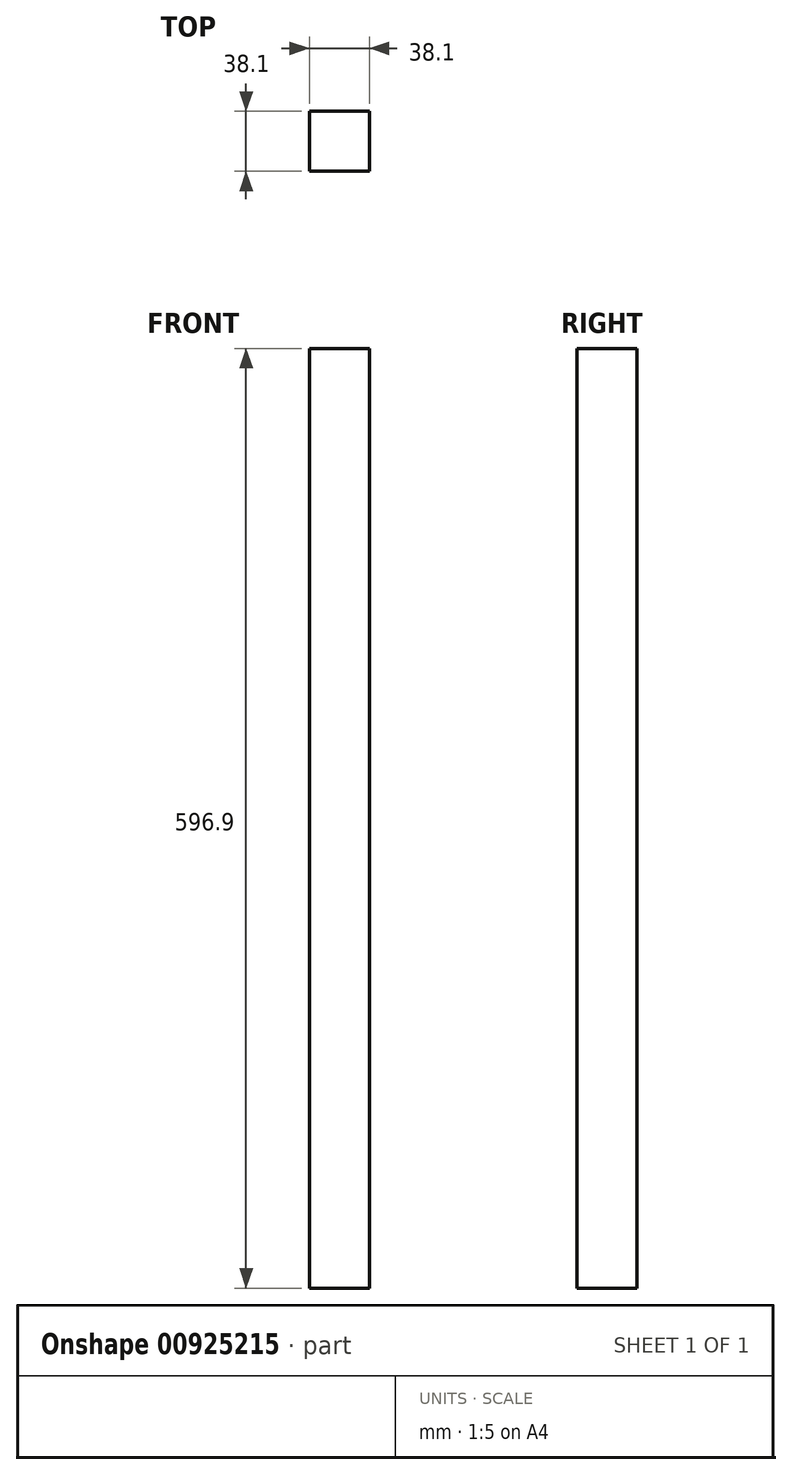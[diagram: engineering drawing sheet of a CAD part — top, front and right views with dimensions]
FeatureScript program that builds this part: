
annotation { "Feature Type Name" : "Feature", "Feature Type Description" : "" }
export const myFeature = defineFeature(function(context is Context, id is Id, definition is map)
    precondition{}
    {
        {
            var Q0;
            Q0=qCreatedBy(makeId("Top.planeOp"),FACE);
            var sketch = newSketch(context, id + "F0", { "sketchPlane" : qUnion([Q0])});
            skLineSegment(sketch, "E0.bottom", {"start": v(19.05, -19.05) * mm, "end": v(-19.05, -19.05) * mm});
            skLineSegment(sketch, "E0.top", {"start": v(19.05, 19.05) * mm, "end": v(-19.05, 19.05) * mm});
            skLineSegment(sketch, "E0.left", {"start": v(19.05, -19.05) * mm, "end": v(19.05, 19.05) * mm});
            skLineSegment(sketch, "E0.right", {"start": v(-19.05, -19.05) * mm, "end": v(-19.05, 19.05) * mm});
            skPoint(sketch, "E0.middle", {"position": v(0, 0) * mm});
            skSolve(sketch);
        }
        {
            var Q0;
            Q0 = qSketchRegion(id + "F0", true);
            extrude(context, id + "F1", {"entities" : qUnion([Q0]), "depth" : 596.9 * mm, "offsetDistance" : 25.4 * mm});
        }
    });
